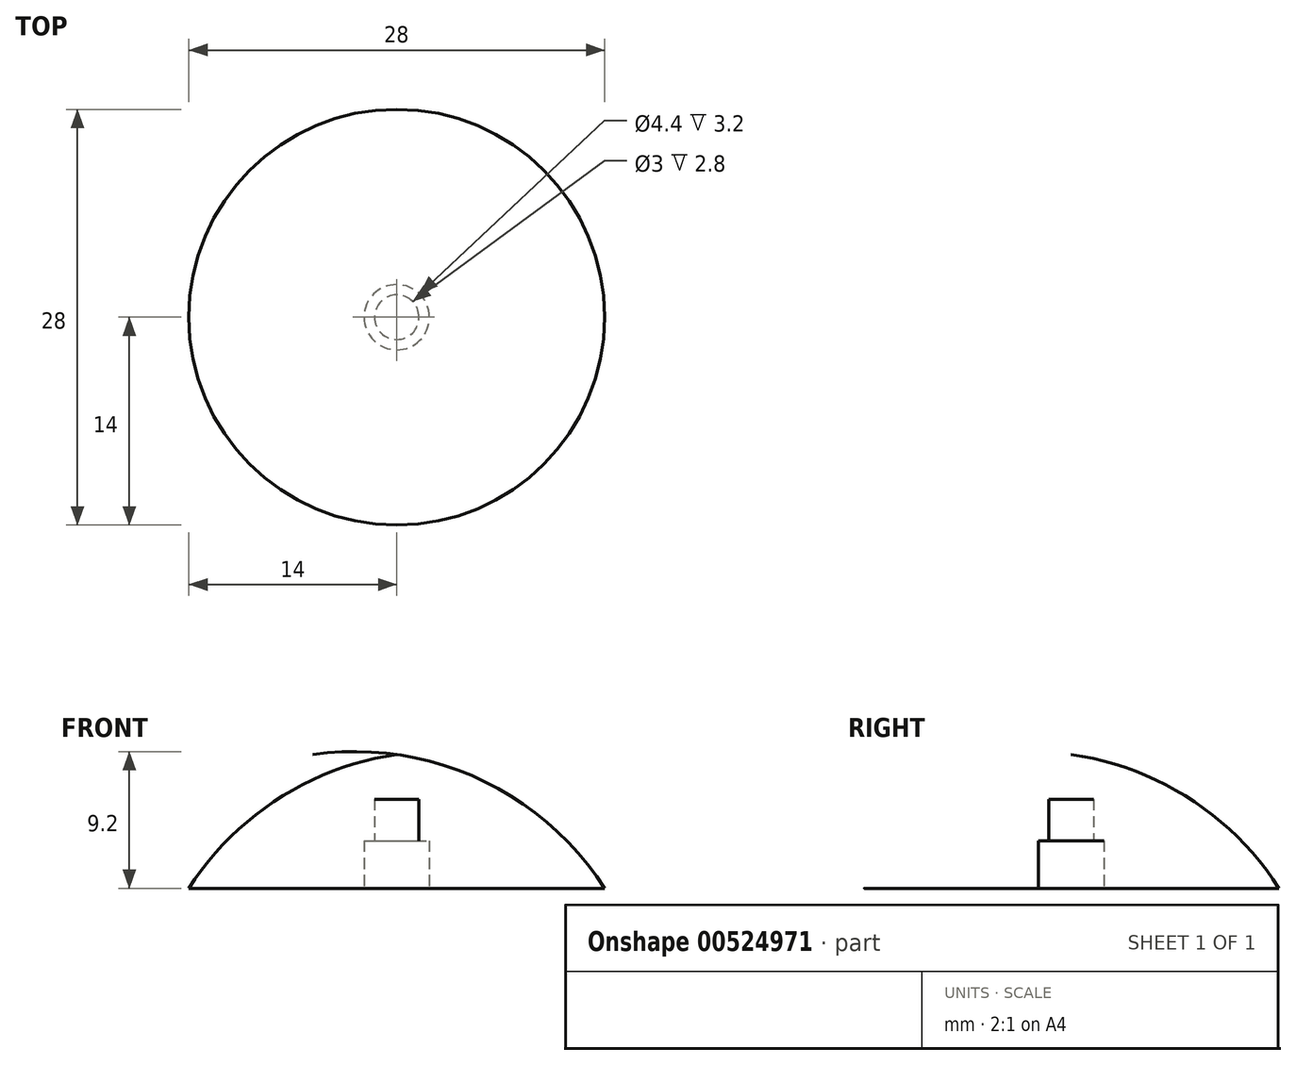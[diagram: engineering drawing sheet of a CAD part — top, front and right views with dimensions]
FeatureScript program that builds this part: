
annotation { "Feature Type Name" : "Feature", "Feature Type Description" : "" }
export const myFeature = defineFeature(function(context is Context, id is Id, definition is map)
    precondition{}
    {
        {
            var Q0;
            Q0=qCreatedBy(makeId("Right.planeOp"),FACE);
            var sketch = newSketch(context, id + "F0", { "sketchPlane" : qUnion([Q0])});
            skLineSegment(sketch, "E0", {"start": v(-2.2, 0) * mm, "end": v(-14, 0) * mm});
            skLineSegment(sketch, "E1", {"start": v(0, 6) * mm, "end": v(0, 9) * mm});
            skArc(sketch, "E2", {"start": v(0, 9) * mm, "mid": v(-7.98, 6.03) * mm, "end": v(-14, 0) * mm});
            skLineSegment(sketch, "E3", {"start": v(0, 6) * mm, "end": v(-1.5, 6) * mm});
            skLineSegment(sketch, "E4", {"start": v(-1.5, 6) * mm, "end": v(-1.5, 3.2) * mm});
            skLineSegment(sketch, "E5", {"start": v(0, 6.87) * mm, "end": v(0, 0) * mm, "construction": true});
            skLineSegment(sketch, "E6", {"start": v(-1.5, 3.2) * mm, "end": v(-2.2, 3.2) * mm});
            skLineSegment(sketch, "E7", {"start": v(-2.2, 3.2) * mm, "end": v(-2.2, 0) * mm});
            skSolve(sketch);
        }
        {
            var Q0;
            Q0=makeQuery(id+"F0.imprint","IMPRINT",FACE,{"disambiguationData":[TD([[makeQuery(id+"F0.imprint","IMPRINT",EDGE,{"derivedFrom":sQuery(id+"F0.wireOp",EDGE,"E0")}),-1.0]])]});
            var Q1;
            Q1=sQuery(id+"F0.wireOp",EDGE,"E1");
            revolve(context, id + "F1", {"entities" : qUnion([Q0]), "axis" : qUnion([Q1]), "revolveType" : RevolveType.FULL});
        }
    });
